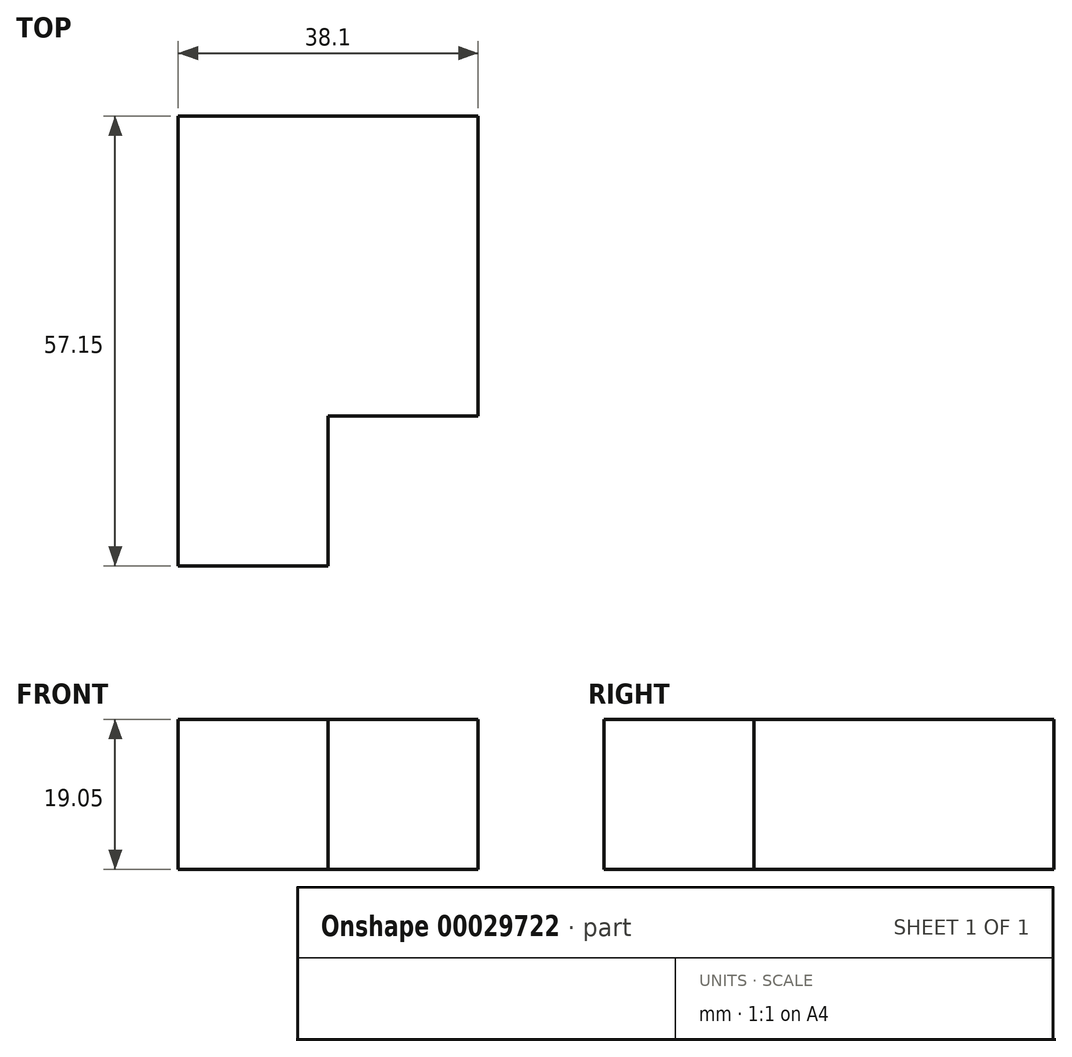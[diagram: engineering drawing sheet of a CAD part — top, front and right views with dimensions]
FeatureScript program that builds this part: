
annotation { "Feature Type Name" : "Feature", "Feature Type Description" : "" }
export const myFeature = defineFeature(function(context is Context, id is Id, definition is map)
    precondition{}
    {
        {
            var Q0;
            Q0=qCreatedBy(makeId("Top.planeOp"),FACE);
            var sketch = newSketch(context, id + "F0", { "sketchPlane" : qUnion([Q0])});
            skLineSegment(sketch, "E0.bottom", {"start": v(-62.07, -57.15) * mm, "end": v(-43.02, -57.15) * mm});
            skLineSegment(sketch, "E0.top", {"start": v(-62.07, 0) * mm, "end": v(-43.02, 0) * mm});
            skLineSegment(sketch, "E0.left", {"start": v(-62.07, -57.15) * mm, "end": v(-62.07, 0) * mm});
            skLineSegment(sketch, "E0.right", {"start": v(-43.02, -57.15) * mm, "end": v(-43.02, 0) * mm});
            skLineSegment(sketch, "E1.bottom", {"start": v(-43.02, 0) * mm, "end": v(-23.97, 0) * mm});
            skLineSegment(sketch, "E1.top", {"start": v(-43.02, -38.1) * mm, "end": v(-23.97, -38.1) * mm});
            skLineSegment(sketch, "E1.left", {"start": v(-43.02, 0) * mm, "end": v(-43.02, -38.1) * mm});
            skLineSegment(sketch, "E1.right", {"start": v(-23.97, 0) * mm, "end": v(-23.97, -38.1) * mm});
            skSolve(sketch);
        }
        {
            var Q0;
            Q0 = qSketchRegion(id + "F0", true);
            extrude(context, id + "F1", {"entities" : qUnion([Q0]), "depth" : 19.05 * mm});
        }
    });
